# Revit family: 1965 Tableau Coffee Table
name_source: partatom
category: Furniture
revit_build: Autodesk Revit 2017 (Build: 20171027_0315(x64)
units: mm (PartAtom-declared; Revit-internal decimal feet)

## family parameters
Always vertical = Yes
Cut with Voids When Loaded = No
OmniClass Number = 23.40.20.00
OmniClass Title = General Furniture and Specialties
Room Calculation Point = No
Shared = No
Work Plane-Based = No

## types (1)
- 1965 Tableau Coffee Table
    Description = The Tableau series in stone reflects a passion for natural materials that runs deep in our DNA, involving expert craftmanship that lies at the core of our company. With its graceful geometric contours and x-shaped base, Tableau creates a soft silhouette that exudes effortless elegance.
    Design year = 2019
    Designer = Space Copenhagen
    Frame = FF Dark Atlantico Limestone
    Height = 40 cm
    Item No. = 1965
    Length = 140 cm
    Manufacturer = Fredericia Furniture
    Model = Tableau Coffee Table
    Table Top = FF Dark Atlantico Limestone
    URL = https://www.fredericia.com
    Weight = 152 kg
    Width = 140 cm

## geometry (parser evidence)
native form markers: Sweep x3
no freeform markers — native parametric forms only
